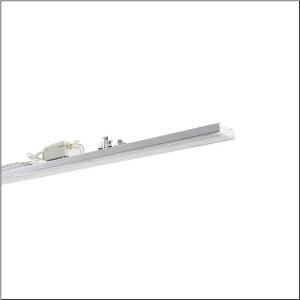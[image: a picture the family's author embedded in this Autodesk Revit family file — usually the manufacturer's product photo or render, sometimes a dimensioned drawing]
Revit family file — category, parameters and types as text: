
# Revit family: licross_r__21_recessed_mo_52te12dv4fxg3s_e0fc
name_source: partatom
category: Lighting Fixtures
units: mm (PartAtom-declared; Revit-internal decimal feet)

## family parameters
Cut with Voids When Loaded = No
Host = Face
Light Source = No
Part Type = Normal
Room Calculation Point = No
Round Connector Dimension = Use Diameter
Shared = No

## types (1)
- --- (1 x LED, 950 lm, 5.5 W, 4000K)
    Apparent Load = 6 VA
    CIE Flux Codes = 72 92 99 100 100
    Color Rendering = 80
    Color Temperature = 4000K
    Default Elevation = 1800 mm
    Description = Licross® 21 Recessed MO, luminaire insert, of sheet steel, galvanised, coil coated, white, length: 2.250mm, width: 66mm, height: 67mm, LED rated luminous flux: 15.420lm, light colour: 840, control gear: DALI 2, with plug, 6-pole, with phase selection, for trunking rail, 14-core, mains connection: 220..240V, AC, 50/60Hz, rated input power: 89W, for trunking rail, 14-core, halogen-free wiring, for emergency light function, converter,control gear: single battery element, battery: LiFeP04, 9Ah, primary optical cover: cover, of PMMA, light emission: direct distribution, primary light characteristic: symmetric, protection rating (complete): IP54, insulation class (complete): insulation class I (protective earthing), certification: CE, UKCA, protection symbol: D if used in an environment with non-conductive dust loads with corresponding accessories, impact resistance: IK06, permissible ambient temperature for indoor applications: +5..+35°C, standard: EN 60598-2-22, LABS conformity tested according to VDMA 24364:2018-05, reducing of maximum allowable ambient temperature of 5°C with ceiling mounting, corresponds to IFS (International Featured Standards) requirements for safety and quality in the food industry, packaging unit: 1 piece
    Height = 58 mm
    Lamp = 1 x LED
    Lamp Light Flux = 950 lm
    Lamp Power = 5.5 W
    Lamp count = 1
    Length = 2250 mm
    Luminous efficacy = 173 lm/W
    Manufacturer = Siteco
    ModVariant = No
    Model = 52TE12DV4FXG3S
    Mounting Place = Ceiling
    Mounting Type = Pendant
    Number of Poles = 1
    OnlyDefault = Yes
    Power Factor = 1
    Product Name = Licross® 21 Recessed MO
    Product group = luminaire insert
    ProductGroupID = 901
    Protection Class = Protection class I
    Protection Degree = IP 54
    RLX_Detail_Level = 1
    RLX_Emergency_Light_Flux = 0 lm
    RLX_Emergency_Type = 0
    RLX_Emergency_Type_DB = No
    RlxData = <blob elided: 29925 chars, md5=45321b54>
    Socket = socket
    Standby Power = 0 W
    System Light Flux = 950 lm
    System Power = 6 W
    Type Comments = : emergency light operation: 3 h
    Type Image = l_1296930.jpg
    URL = http://relux.com
    VarID = @adj_040197
    Voltage = 0 V
    Weight = 0.00 kg
    Width = 66 mm

## geometry (parser evidence)
native form markers: Blend x4, Sweep x9
no freeform markers — native parametric forms only
